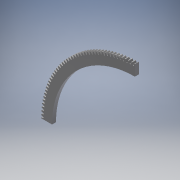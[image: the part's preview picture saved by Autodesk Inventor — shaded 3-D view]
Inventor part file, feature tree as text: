
AUTODESK INVENTOR PART (.ipt)
format: ipt  version: 2017 (Build 210142000, 142)  size: 596,992 bytes
history: native  units: mm (DEFAULTED — no unit token found)
features: sketch x4, extrude x3, plane x3, other x3
ambient origin geometry x8: Origin, YZ Plane, XZ Plane, XY Plane, X Axis, Y Axis, Z Axis, Center Point
bodies: Solid1 (feature_tree)
feature tree (13):
  extrude  "Extrusion1"  Depth=6.35mm TaperAngle=0.0deg
  plane  "Work Plane1"
  plane  "Work Plane2"
  plane  "Work Plane3"
  other  "Spur Gear"
  extrude  "Extrusion2"  Depth=76.2mm TaperAngle=0.0deg
  extrude  "Extrusion3"  TaperAngle=0.0deg  [1 undecoded]
  sketch  "Sketch1"  dims[d0=301.413333mm d1=6.35mm d2=0.0mm]
  sketch  "Sketch2"  dims[d3=298.026667mm d4=76.2mm d5=0.0mm]
  other  "Srf1"
  sketch  "Sketch3"  dims[d6=0.0mm d7=0.1785mm d9=0.0mm]
  sketch  "Sketch4"  dims[d14=0.0mm d15=161.713333mm d16=0.0mm d17=0.0mm d18=0.0mm d19=161.713333mm d20=266.421792mm d21=25.4mm d22=0.0mm d23=0.0mm d24=0.0mm]
  other  "Pitch Diameter"
note: 1 required parameter value undecoded (feature->parameter linkage not recoverable at this tier; creation-order binding heuristic only, values carry confidence <= 0.55)
